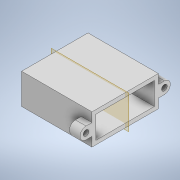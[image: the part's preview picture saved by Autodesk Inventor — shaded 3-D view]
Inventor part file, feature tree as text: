
AUTODESK INVENTOR PART (.ipt)
format: ipt  version: 2021 (Build 250183000, 183)  size: 162,816 bytes
history: native  units: mm
features: extrude x4, sketch x3, projected_geometry x2, mirror x1
ambient origin geometry x8: Origin, YZ Plane, XZ Plane, XY Plane, X Axis, Y Axis, Z Axis, Center Point
bodies: Body1 (feature_tree)
feature tree (10):
  sketch  "Sketch2"  dims[d8=50.0mm d9=23.0mm]
  extrude  "Extrusion3"  Depth=23.0mm
  extrude  "Extrusion4"  Depth=3.0mm
  extrude  "Extrusion7"  Depth=17.0mm
  extrude  "Extrusion8"  Depth=3.0mm TaperAngle=0.0deg
  mirror  "Mirror1"
  sketch  "Sketch5"  dims[d10=3.0mm d11=3.0mm]
  projected_geometry  "Projected Loop3"
  sketch  "Sketch6"  dims[d12=3.0mm d13=17.0mm d14=3.0mm d15=0.0mm d16=53.0mm d17=0.0mm d32=9.0mm d33=4.5mm d34=8.0mm d35=0.0mm d36=6.2mm d37=4.0mm d38=0.0mm d39=4.2mm]
  projected_geometry  "Projected Loop4"
